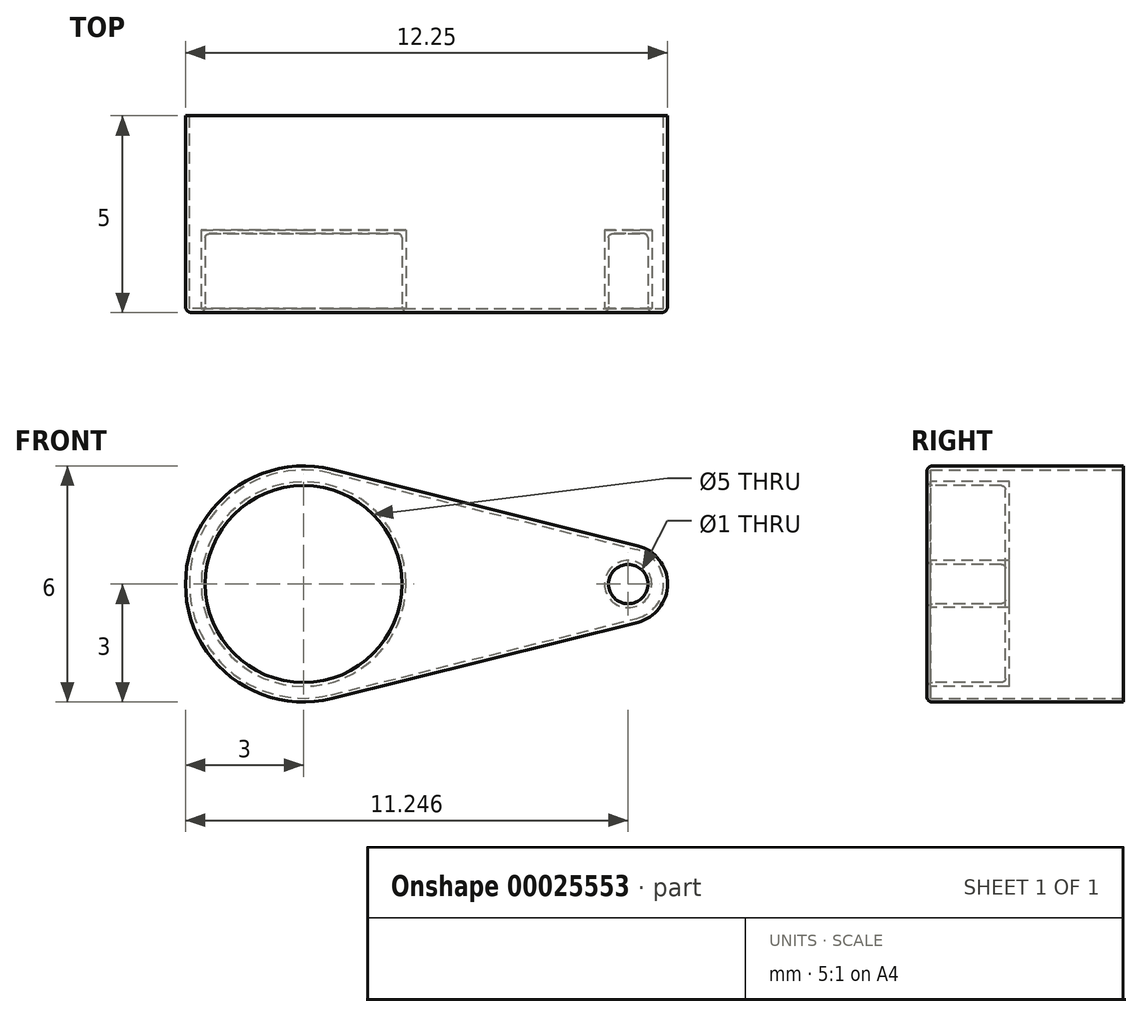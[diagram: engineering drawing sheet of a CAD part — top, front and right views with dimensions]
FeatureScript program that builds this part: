
annotation { "Feature Type Name" : "Feature", "Feature Type Description" : "" }
export const myFeature = defineFeature(function(context is Context, id is Id, definition is map)
    precondition{}
    {
        {
            var Q0;
            Q0=qCreatedBy(makeId("Front.planeOp"),FACE);
            var sketch = newSketch(context, id + "F0", { "sketchPlane" : qUnion([Q0])});
            skCircle(sketch, "E0", {"center": v(0, 0) * mm, "radius": 3 * mm});
            skCircle(sketch, "E1", {"center": v(8.25, 0) * mm, "radius": 1 * mm});
            skLineSegment(sketch, "E2", {"start": v(0.73, 2.91) * mm, "end": v(8.49, 0.97) * mm});
            skLineSegment(sketch, "E3", {"start": v(0.73, -2.91) * mm, "end": v(8.49, -0.97) * mm});
            skSolve(sketch);
        }
        {
            var Q0;
            {var subQ0=sQuery(id+"F0.wireOp",EDGE,"E0");var subQ2=makeQuery(id+"F0.imprint","INTERSECT",VERTEX,{"derivedFrom":[subQ0,sQuery(id+"F0.wireOp",EDGE,"E2")]});Q0=makeQuery(id+"F0.imprint","IMPRINT",FACE,{"disambiguationData":[TD([[makeQuery(id+"F0.imprint","IMPRINT",EDGE,{"disambiguationData":[TD([[subQ2,-1.0]])],"derivedFrom":subQ0}),1.0]])]});}
            var Q1;
            {var subQ1=sQuery(id+"F0.wireOp",EDGE,"E2");Q1=makeQuery(id+"F0.imprint","IMPRINT",FACE,{"disambiguationData":[TD([[makeQuery(id+"F0.imprint","IMPRINT",EDGE,{"derivedFrom":subQ1}),-1.0]])]});}
            var Q2;
            {var subQ0=sQuery(id+"F0.wireOp",EDGE,"E1");var subQ2=makeQuery(id+"F0.imprint","INTERSECT",VERTEX,{"derivedFrom":[subQ0,sQuery(id+"F0.wireOp",EDGE,"E2")]});Q2=makeQuery(id+"F0.imprint","IMPRINT",FACE,{"disambiguationData":[TD([[makeQuery(id+"F0.imprint","IMPRINT",EDGE,{"disambiguationData":[TD([[subQ2,-1.0]])],"derivedFrom":subQ0}),1.0]])]});}
            extrude(context, id + "F1", {"entities" : qUnion([Q0, Q1, Q2]), "depth" : 5 * mm});
        }
        {
            var Q0;
            Q0=makeQuery(id+"F1.opExtrude","CAP_FACE",FACE,{"disambiguationData":[OSD([sQuery(id+"F0.wireOp",EDGE,"E0"),sQuery(id+"F0.wireOp",EDGE,"E1"),sQuery(id+"F0.wireOp",EDGE,"E2"),sQuery(id+"F0.wireOp",EDGE,"E3")])],"isStart":false});
            var sketch = newSketch(context, id + "F2", { "sketchPlane" : qUnion([Q0])});
            skCircle(sketch, "E4", {"center": v(0, 0) * mm, "radius": 2.5 * mm});
            skCircle(sketch, "E5", {"center": v(8.25, 0) * mm, "radius": 0.5 * mm});
            skSolve(sketch);
        }
        {
            var Q0;
            Q0=makeQuery(id+"F2.imprint","IMPRINT",FACE,{"disambiguationData":[TD([[makeQuery(id+"F2.imprint","IMPRINT",EDGE,{"derivedFrom":sQuery(id+"F2.wireOp",EDGE,"E5")}),1.0]])]});
            var Q1;
            Q1=makeQuery(id+"F2.imprint","IMPRINT",FACE,{"disambiguationData":[TD([[makeQuery(id+"F2.imprint","IMPRINT",EDGE,{"derivedFrom":sQuery(id+"F2.wireOp",EDGE,"E4")}),1.0]])]});
            extrude(context, id + "F3", {"entities" : qUnion([Q0, Q1]), "operationType" : NewBodyOperationType.REMOVE, "oppositeDirection" : true, "depth" : 2 * mm});
        }
        {
            var Q0;
            Q0=makeQuery(id+"F1.opExtrude","CAP_FACE",FACE,{"disambiguationData":[OSD([sQuery(id+"F0.wireOp",EDGE,"E0"),sQuery(id+"F0.wireOp",EDGE,"E1"),sQuery(id+"F0.wireOp",EDGE,"E2"),sQuery(id+"F0.wireOp",EDGE,"E3")])],"isStart":true});
            shell(context, id + "F4", {"entities" : qUnion([Q0]), "thickness" : .1 * mm});
        }
        {
            var Q0;
            Q0=makeQuery(id+"F1.opExtrude","CAP_FACE",FACE,{"disambiguationData":[OSD([sQuery(id+"F0.wireOp",EDGE,"E0"),sQuery(id+"F0.wireOp",EDGE,"E1"),sQuery(id+"F0.wireOp",EDGE,"E2"),sQuery(id+"F0.wireOp",EDGE,"E3")])],"isStart":false});
            fillet(context, id + "F5", {"entities" : qUnion([Q0]), "radius" : .15 * mm, "tangentPropagation" : true, "allowEdgeOverflow" : false});
        }
        {
            var Q0;
            Q0=makeQuery(id+"F3.boolean.opBoolean","COPY",FACE,{"derivedFrom":makeQuery(id+"F3.opExtrude","CAP_FACE",FACE,{"disambiguationData":[OSD([sQuery(id+"F2.wireOp",EDGE,"E4")])],"isStart":false})});
            var Q1;
            Q1=makeQuery(id+"F3.boolean.opBoolean","COPY",FACE,{"derivedFrom":makeQuery(id+"F3.opExtrude","CAP_FACE",FACE,{"disambiguationData":[OSD([sQuery(id+"F2.wireOp",EDGE,"E5")])],"isStart":false})});
            fillet(context, id + "F6", {"entities" : qUnion([Q0, Q1]), "radius" : .1 * mm, "tangentPropagation" : true, "allowEdgeOverflow" : false});
        }
    });
